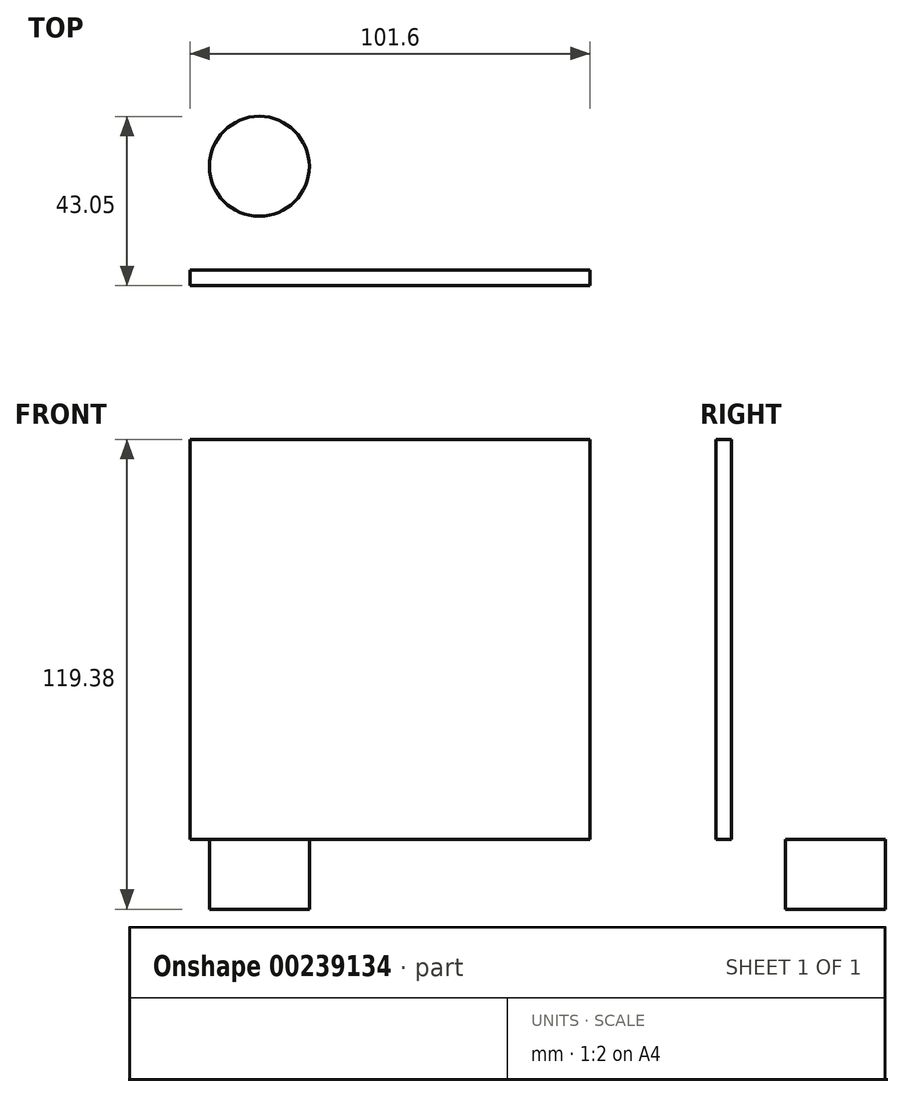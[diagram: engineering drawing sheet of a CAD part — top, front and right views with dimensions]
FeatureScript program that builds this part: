
annotation { "Feature Type Name" : "Feature", "Feature Type Description" : "" }
export const myFeature = defineFeature(function(context is Context, id is Id, definition is map)
    precondition{}
    {
        {
            assignVariable(context, id + "F0", {"name" : "F", "anyValue" : 4});
        }
        {
            var Q0;
            Q0=qCreatedBy(makeId("Front.planeOp"),FACE);
            var sketch = newSketch(context, id + "F1", { "sketchPlane" : qUnion([Q0])});
            skLineSegment(sketch, "E0.bottom", {"start": v(-50.8, -50.8) * mm, "end": v(50.8, -50.8) * mm});
            skLineSegment(sketch, "E0.top", {"start": v(-50.8, 50.8) * mm, "end": v(50.8, 50.8) * mm});
            skLineSegment(sketch, "E0.left", {"start": v(-50.8, -50.8) * mm, "end": v(-50.8, 50.8) * mm});
            skLineSegment(sketch, "E0.right", {"start": v(50.8, -50.8) * mm, "end": v(50.8, 50.8) * mm});
            skPoint(sketch, "E0.middle", {"position": v(0, 0) * mm});
            skSolve(sketch);
        }
        {
            var Q0;
            Q0 = qSketchRegion(id + "F1", true);
            extrude(context, id + "F2", {"entities" : qUnion([Q0]), "endBound" : BoundingType.SYMMETRIC, "depth" : (getVariable(context, 'F')) * mm});
        }
        {
            var Q0;
            Q0=makeQuery(id+"F2.opExtrude","SWEPT_FACE",FACE,{"disambiguationData":[OSD([sQuery(id+"F1.wireOp",EDGE,"E0.top")])]});
            var sketch = newSketch(context, id + "F3", { "sketchPlane" : qUnion([Q0])});
            skCircle(sketch, "E1", {"center": v(-33.21, 28.35) * mm, "radius": 12.7 * mm});
            skSolve(sketch);
        }
        {
            var Q0;
            Q0=makeQuery(id+"F3.imprint","IMPRINT",FACE,{"disambiguationData":[TD([[makeQuery(id+"F3.imprint","IMPRINT",EDGE,{"derivedFrom":sQuery(id+"F3.wireOp",EDGE,"E1")}),1.0]])]});
            extrude(context, id + "F4", {"entities" : qUnion([Q0]), "operationType" : NewBodyOperationType.REMOVE, "oppositeDirection" : true, "depth" : 25.4 * mm});
        }
        {
            var Q0;
            Q0=makeQuery(id+"F2.opExtrude","SWEPT_FACE",FACE,{"disambiguationData":[OSD([sQuery(id+"F1.wireOp",EDGE,"E0.bottom")])]});
            var sketch = newSketch(context, id + "F5", { "sketchPlane" : qUnion([Q0])});
            skCircle(sketch, "E2.0", {"center": v(-33.21, -28.35) * mm, "radius": 12.7 * mm});
            skSolve(sketch);
        }
        {
            var Q0;
            Q0=makeQuery(id+"F5.imprint","IMPRINT",FACE,{"disambiguationData":[TD([[makeQuery(id+"F5.imprint","IMPRINT",EDGE,{"derivedFrom":sQuery(id+"F5.wireOp",EDGE,"E2.0")}),1.0]])]});
            extrude(context, id + "F6", {"entities" : qUnion([Q0]), "operationType" : NewBodyOperationType.ADD, "depth" : 17.78 * mm});
        }
    });
